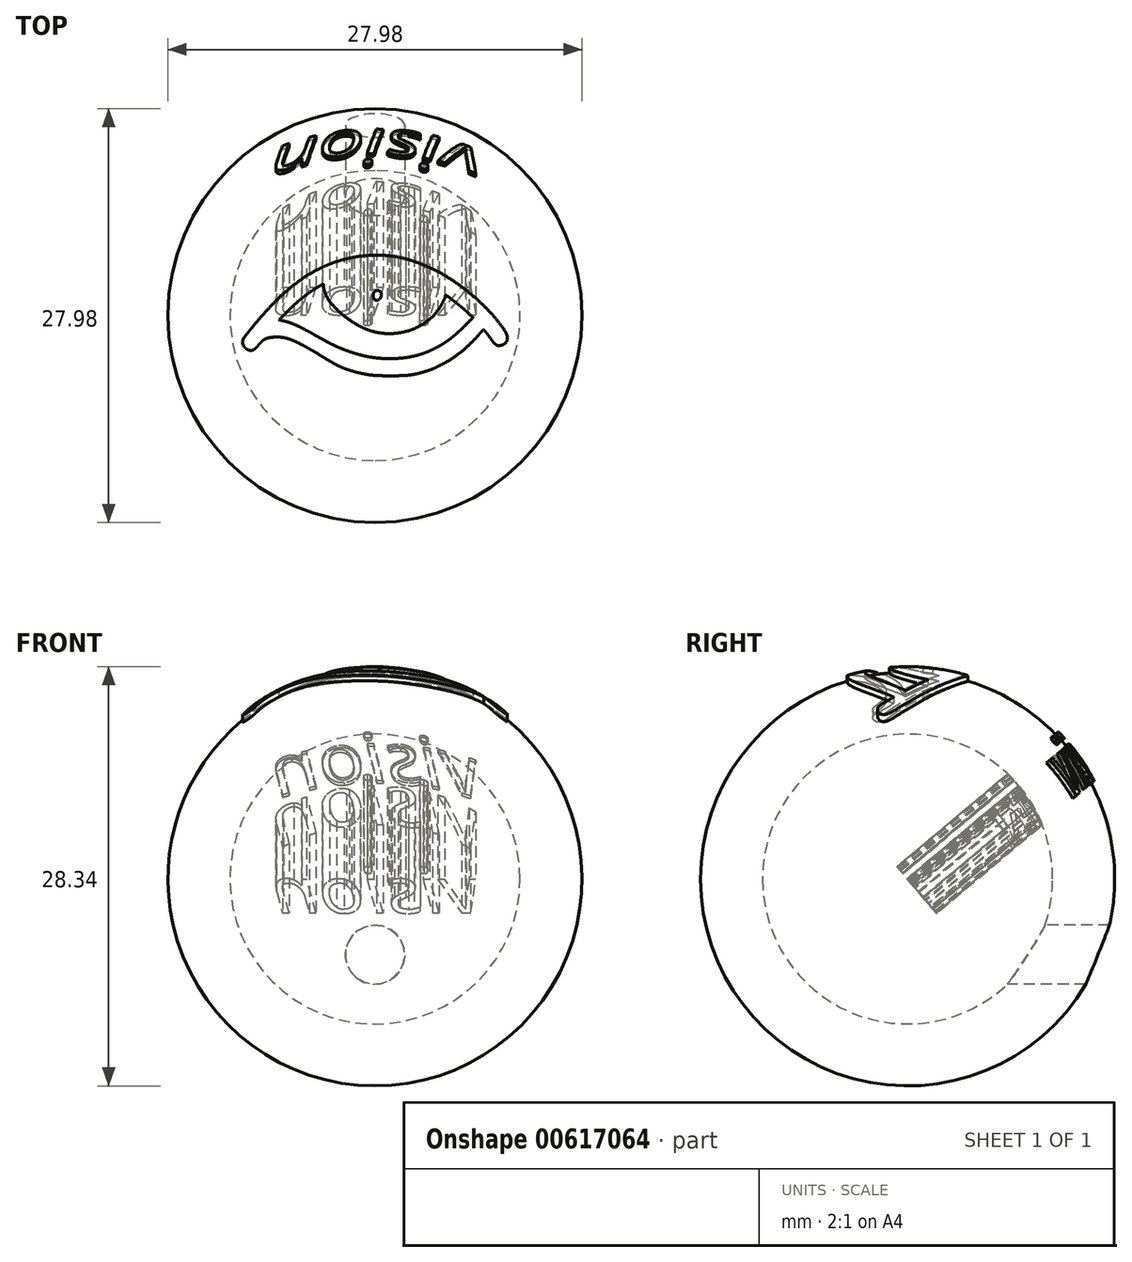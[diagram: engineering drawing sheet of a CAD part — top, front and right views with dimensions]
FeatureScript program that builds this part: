
annotation { "Feature Type Name" : "Feature", "Feature Type Description" : "" }
export const myFeature = defineFeature(function(context is Context, id is Id, definition is map)
    precondition{}
    {
        {
            var Q0;
            Q0=qCreatedBy(makeId("Top.planeOp"),FACE);
            var sketch = newSketch(context, id + "F0", { "sketchPlane" : qUnion([Q0])});
            skLineSegment(sketch, "E0", {"start": v(0, -10) * mm, "end": v(0, 10) * mm});
            skArc(sketch, "E1", {"start": v(0, 10) * mm, "mid": v(-10, 0) * mm, "end": v(0, -10) * mm});
            skSolve(sketch);
        }
        {
            var Q0;
            {var subQ0=sQuery(id+"F0.wireOp",EDGE,"E1");Q0=makeQuery(id+"F0.imprint","IMPRINT",FACE,{"disambiguationData":[TD([[makeQuery(id+"F0.imprint","IMPRINT",EDGE,{"derivedFrom":subQ0}),1.0]])]});}
            var Q1;
            Q1=sQuery(id+"F0.wireOp",EDGE,"E0");
            revolve(context, id + "F1", {"entities" : qUnion([Q0]), "axis" : qUnion([Q1]), "revolveType" : RevolveType.FULL});
        }
        {
            var Q0;
            Q0=makeQuery(id+"F1.opRevolve","SWEPT_BODY",BODY,{"disambiguationData":[OSD([sQuery(id+"F0.wireOp",EDGE,"E0"),sQuery(id+"F0.wireOp",EDGE,"E1")])]});
            var Q1;
            Q1=sQuery(id+"F0.wireOp",VERTEX,"NPe4G0ez-t7S9-9isL-QO5v-uuJu600mHcIT.center");
            var Q2;
            Q2=sQuery(id+"F0.wireOp",VERTEX,"E1.center");
            transform(context, id + "F2", {"entities" : qUnion([Q0]), "transformType" : TransformType.SCALE_UNIFORMLY, "scale" : 33.3, "scalePoint" : qUnion([Q2]), "makeCopy" : false});
        }
        {
            var Q0;
            Q0=qCreatedBy(makeId("Top.planeOp"),FACE);
            var sketch = newSketch(context, id + "F3", { "sketchPlane" : qUnion([Q0])});
            skArc(sketch, "E2", {"start": v(-15.7, 96.27) * mm, "mid": v(-24.88, 95.28) * mm, "end": v(-34, 93.81) * mm});
            skArc(sketch, "E3", {"start": v(-34, 93.81) * mm, "mid": v(-43.55, 91.8) * mm, "end": v(-53.01, 89.37) * mm});
            skArc(sketch, "E4", {"start": v(-53.01, 89.37) * mm, "mid": v(-62.4, 86.52) * mm, "end": v(-71.64, 83.27) * mm});
            skArc(sketch, "E5", {"start": v(-71.64, 83.27) * mm, "mid": v(-80.3, 79.75) * mm, "end": v(-88.77, 75.81) * mm});
            skArc(sketch, "E6", {"start": v(-88.77, 75.81) * mm, "mid": v(-102.81, 68.2) * mm, "end": v(-116.28, 59.63) * mm});
            skArc(sketch, "E7", {"start": v(-116.28, 59.63) * mm, "mid": v(-129.86, 49.68) * mm, "end": v(-142.83, 38.92) * mm});
            skArc(sketch, "E8", {"start": v(-142.83, 38.92) * mm, "mid": v(-156.87, 25.88) * mm, "end": v(-170.22, 12.13) * mm});
            skArc(sketch, "E9", {"start": v(-170.22, 12.13) * mm, "mid": v(-185.55, -5) * mm, "end": v(-200.36, -22.6) * mm});
            skArc(sketch, "E10", {"start": v(-200.36, -22.6) * mm, "mid": v(-204.26, -27.4) * mm, "end": v(-208.11, -32.22) * mm});
            skArc(sketch, "E11", {"start": v(-208.11, -32.22) * mm, "mid": v(-209.68, -34.33) * mm, "end": v(-211.1, -36.54) * mm});
            skArc(sketch, "E12", {"start": v(-211.1, -36.54) * mm, "mid": v(-211.9, -38.1) * mm, "end": v(-212.43, -39.77) * mm});
            skArc(sketch, "E13", {"start": v(-212.43, -39.77) * mm, "mid": v(-212.77, -41.62) * mm, "end": v(-212.89, -43.5) * mm});
            skArc(sketch, "E14", {"start": v(-212.89, -43.5) * mm, "mid": v(-212.7, -45.36) * mm, "end": v(-212.17, -47.16) * mm});
            skArc(sketch, "E15", {"start": v(-212.17, -47.16) * mm, "mid": v(-211.25, -49.03) * mm, "end": v(-210.08, -50.75) * mm});
            skArc(sketch, "E16", {"start": v(-210.08, -50.75) * mm, "mid": v(-208.63, -52.35) * mm, "end": v(-206.98, -53.74) * mm});
            skArc(sketch, "E17", {"start": v(-206.98, -53.74) * mm, "mid": v(-205.23, -54.82) * mm, "end": v(-203.34, -55.62) * mm});
            skArc(sketch, "E18", {"start": v(-203.34, -55.62) * mm, "mid": v(-201.34, -56.09) * mm, "end": v(-199.3, -56.2) * mm});
            skArc(sketch, "E19", {"start": v(-199.3, -56.2) * mm, "mid": v(-197.43, -55.94) * mm, "end": v(-195.66, -55.27) * mm});
            skArc(sketch, "E20", {"start": v(-195.66, -55.27) * mm, "mid": v(-193.67, -54.05) * mm, "end": v(-191.9, -52.53) * mm});
            skArc(sketch, "E21", {"start": v(-191.9, -52.53) * mm, "mid": v(-189.54, -50.04) * mm, "end": v(-187.31, -47.43) * mm});
            skArc(sketch, "E22", {"start": v(-187.31, -47.43) * mm, "mid": v(-184.58, -44.29) * mm, "end": v(-181.61, -41.36) * mm});
            skArc(sketch, "E23", {"start": v(-181.61, -41.36) * mm, "mid": v(-179.01, -39.32) * mm, "end": v(-176.14, -37.68) * mm});
            skArc(sketch, "E24", {"start": v(-176.14, -37.68) * mm, "mid": v(-172.97, -36.44) * mm, "end": v(-169.65, -35.65) * mm});
            skArc(sketch, "E25", {"start": v(-169.65, -35.65) * mm, "mid": v(-165.2, -35.07) * mm, "end": v(-160.72, -34.76) * mm});
            skArc(sketch, "E26", {"start": v(-160.72, -34.76) * mm, "mid": v(-158.15, -34.7) * mm, "end": v(-155.59, -34.7) * mm});
            skArc(sketch, "E27", {"start": v(-155.59, -34.7) * mm, "mid": v(-153.46, -34.78) * mm, "end": v(-151.33, -34.94) * mm});
            skArc(sketch, "E28", {"start": v(-151.33, -34.94) * mm, "mid": v(-149.29, -35.18) * mm, "end": v(-147.26, -35.51) * mm});
            skArc(sketch, "E29", {"start": v(-147.26, -35.51) * mm, "mid": v(-144.98, -35.98) * mm, "end": v(-142.72, -36.5) * mm});
            skArc(sketch, "E30", {"start": v(-142.72, -36.5) * mm, "mid": v(-137.7, -37.98) * mm, "end": v(-132.83, -39.85) * mm});
            skArc(sketch, "E31", {"start": v(-132.83, -39.85) * mm, "mid": v(-126.18, -42.83) * mm, "end": v(-119.62, -46) * mm});
            skArc(sketch, "E32", {"start": v(-119.62, -46) * mm, "mid": v(-111.94, -50) * mm, "end": v(-104.36, -54.22) * mm});
            skArc(sketch, "E33", {"start": v(-104.36, -54.22) * mm, "mid": v(-96.08, -59.09) * mm, "end": v(-87.89, -64.12) * mm});
            skArc(sketch, "E34", {"start": v(-87.89, -64.12) * mm, "mid": v(-78.64, -69.83) * mm, "end": v(-69.3, -75.4) * mm});
            skArc(sketch, "E35", {"start": v(-69.3, -75.4) * mm, "mid": v(-62.78, -79.02) * mm, "end": v(-56.09, -82.33) * mm});
            skArc(sketch, "E36", {"start": v(-56.09, -82.33) * mm, "mid": v(-50.08, -84.92) * mm, "end": v(-43.94, -87.15) * mm});
            skArc(sketch, "E37", {"start": v(-43.94, -87.15) * mm, "mid": v(-36.7, -89.4) * mm, "end": v(-29.39, -91.38) * mm});
            skArc(sketch, "E38", {"start": v(-29.39, -91.38) * mm, "mid": v(-22.75, -92.95) * mm, "end": v(-16.08, -94.33) * mm});
            skArc(sketch, "E39", {"start": v(-16.08, -94.33) * mm, "mid": v(-10.4, -95.3) * mm, "end": v(-4.68, -96.02) * mm});
            skArc(sketch, "E40", {"start": v(-4.68, -96.02) * mm, "mid": v(1.7, -96.55) * mm, "end": v(8.07, -96.83) * mm});
            skArc(sketch, "E41", {"start": v(8.07, -96.83) * mm, "mid": v(17.1, -97) * mm, "end": v(26.11, -97.06) * mm});
            skArc(sketch, "E42", {"start": v(26.11, -97.06) * mm, "mid": v(34.81, -96.98) * mm, "end": v(43.5, -96.78) * mm});
            skArc(sketch, "E43", {"start": v(43.5, -96.78) * mm, "mid": v(49.38, -96.48) * mm, "end": v(55.24, -95.93) * mm});
            skArc(sketch, "E44", {"start": v(55.24, -95.93) * mm, "mid": v(60.42, -95.18) * mm, "end": v(65.57, -94.17) * mm});
            skArc(sketch, "E45", {"start": v(65.57, -94.17) * mm, "mid": v(71.73, -92.68) * mm, "end": v(77.85, -91.01) * mm});
            skArc(sketch, "E46", {"start": v(77.85, -91.01) * mm, "mid": v(89.65, -87.08) * mm, "end": v(101.1, -82.22) * mm});
            skArc(sketch, "E47", {"start": v(101.1, -82.22) * mm, "mid": v(112.52, -76.3) * mm, "end": v(123.5, -69.56) * mm});
            skArc(sketch, "E48", {"start": v(123.5, -69.56) * mm, "mid": v(134.48, -61.7) * mm, "end": v(144.89, -53.1) * mm});
            skArc(sketch, "E49", {"start": v(144.89, -53.1) * mm, "mid": v(155.3, -43.34) * mm, "end": v(165.12, -32.98) * mm});
            skLineSegment(sketch, "E50", {"start": v(165.12, -32.98) * mm, "end": v(174.6, -22.4) * mm});
            skLineSegment(sketch, "E51", {"start": v(174.6, -22.4) * mm, "end": v(177.93, -26.25) * mm});
            skArc(sketch, "E52", {"start": v(177.93, -26.25) * mm, "mid": v(178.76, -27.23) * mm, "end": v(179.56, -28.24) * mm});
            skArc(sketch, "E53", {"start": v(179.56, -28.24) * mm, "mid": v(180.69, -29.73) * mm, "end": v(181.8, -31.22) * mm});
            skArc(sketch, "E54", {"start": v(181.8, -31.22) * mm, "mid": v(183.01, -32.88) * mm, "end": v(184.21, -34.54) * mm});
            skArc(sketch, "E55", {"start": v(184.21, -34.54) * mm, "mid": v(185.33, -36.15) * mm, "end": v(186.44, -37.76) * mm});
            skArc(sketch, "E56", {"start": v(186.44, -37.76) * mm, "mid": v(188.89, -41.17) * mm, "end": v(191.53, -44.43) * mm});
            skArc(sketch, "E57", {"start": v(191.53, -44.43) * mm, "mid": v(193.5, -46.3) * mm, "end": v(195.78, -47.72) * mm});
            skArc(sketch, "E58", {"start": v(195.78, -47.72) * mm, "mid": v(197.94, -48.43) * mm, "end": v(200.2, -48.52) * mm});
            skArc(sketch, "E59", {"start": v(200.2, -48.52) * mm, "mid": v(202.97, -48.04) * mm, "end": v(205.62, -47.16) * mm});
            skArc(sketch, "E60", {"start": v(205.62, -47.16) * mm, "mid": v(208.3, -45.62) * mm, "end": v(210.53, -43.46) * mm});
            skArc(sketch, "E61", {"start": v(210.53, -43.46) * mm, "mid": v(212.04, -40.9) * mm, "end": v(212.79, -38.01) * mm});
            skArc(sketch, "E62", {"start": v(212.79, -38.01) * mm, "mid": v(212.79, -34.58) * mm, "end": v(212.02, -31.24) * mm});
            skArc(sketch, "E63", {"start": v(212.02, -31.24) * mm, "mid": v(210.38, -27.4) * mm, "end": v(208.26, -23.82) * mm});
            skArc(sketch, "E64", {"start": v(208.26, -23.82) * mm, "mid": v(196.57, -8.01) * mm, "end": v(183.65, 6.8) * mm});
            skArc(sketch, "E65", {"start": v(183.65, 6.8) * mm, "mid": v(168.5, 21.85) * mm, "end": v(152.44, 35.92) * mm});
            skArc(sketch, "E66", {"start": v(152.44, 35.92) * mm, "mid": v(135.48, 49) * mm, "end": v(117.73, 60.98) * mm});
            skArc(sketch, "E67", {"start": v(117.73, 60.98) * mm, "mid": v(100.55, 70.9) * mm, "end": v(82.64, 79.43) * mm});
            skArc(sketch, "E68", {"start": v(82.64, 79.43) * mm, "mid": v(70.04, 84.47) * mm, "end": v(57.22, 88.9) * mm});
            skArc(sketch, "E69", {"start": v(57.22, 88.9) * mm, "mid": v(45.56, 92.16) * mm, "end": v(33.7, 94.6) * mm});
            skArc(sketch, "E70", {"start": v(33.7, 94.6) * mm, "mid": v(21.92, 96.2) * mm, "end": v(10.05, 96.96) * mm});
            skArc(sketch, "E71", {"start": v(10.05, 96.96) * mm, "mid": v(-2.83, 96.97) * mm, "end": v(-15.7, 96.27) * mm});
            skArc(sketch, "E72", {"start": v(-82.87, 47.15) * mm, "mid": v(-82.82, 46.3) * mm, "end": v(-82.7, 45.47) * mm});
            skArc(sketch, "E73", {"start": v(-82.7, 45.47) * mm, "mid": v(-82.45, 44.2) * mm, "end": v(-82.17, 42.93) * mm});
            skArc(sketch, "E74", {"start": v(-82.17, 42.93) * mm, "mid": v(-81.8, 41.5) * mm, "end": v(-81.41, 40.08) * mm});
            skArc(sketch, "E75", {"start": v(-81.41, 40.08) * mm, "mid": v(-80.99, 38.7) * mm, "end": v(-80.52, 37.33) * mm});
            skArc(sketch, "E76", {"start": v(-80.52, 37.33) * mm, "mid": v(-75.98, 27.48) * mm, "end": v(-69.69, 18.65) * mm});
            skArc(sketch, "E77", {"start": v(-69.69, 18.65) * mm, "mid": v(-60.18, 8.6) * mm, "end": v(-49.8, -0.55) * mm});
            skArc(sketch, "E78", {"start": v(-49.8, -0.55) * mm, "mid": v(-38.08, -9.14) * mm, "end": v(-25.64, -16.65) * mm});
            skArc(sketch, "E79", {"start": v(-25.64, -16.65) * mm, "mid": v(-13.91, -22.11) * mm, "end": v(-1.6, -26.06) * mm});
            skArc(sketch, "E80", {"start": v(-1.6, -26.06) * mm, "mid": v(12.82, -28.6) * mm, "end": v(27.45, -29.03) * mm});
            skArc(sketch, "E81", {"start": v(27.45, -29.03) * mm, "mid": v(42.14, -27.34) * mm, "end": v(56.45, -23.6) * mm});
            skArc(sketch, "E82", {"start": v(56.45, -23.6) * mm, "mid": v(69.79, -17.97) * mm, "end": v(82.17, -10.47) * mm});
            skArc(sketch, "E83", {"start": v(82.17, -10.47) * mm, "mid": v(92.73, -1.58) * mm, "end": v(101.67, 8.94) * mm});
            skArc(sketch, "E84", {"start": v(101.67, 8.94) * mm, "mid": v(103.47, 11.6) * mm, "end": v(105.14, 14.32) * mm});
            skArc(sketch, "E85", {"start": v(105.14, 14.32) * mm, "mid": v(107.13, 17.86) * mm, "end": v(109.03, 21.44) * mm});
            skArc(sketch, "E86", {"start": v(109.03, 21.44) * mm, "mid": v(110.8, 24.92) * mm, "end": v(112.5, 28.44) * mm});
            skArc(sketch, "E87", {"start": v(112.5, 28.44) * mm, "mid": v(112.96, 29.75) * mm, "end": v(113.11, 31.12) * mm});
            skArc(sketch, "E88", {"start": v(113.11, 31.12) * mm, "mid": v(113.13, 31.37) * mm, "end": v(113.17, 31.61) * mm});
            skArc(sketch, "E89", {"start": v(113.17, 31.61) * mm, "mid": v(113.24, 31.83) * mm, "end": v(113.34, 32.03) * mm});
            skArc(sketch, "E90", {"start": v(113.34, 32.03) * mm, "mid": v(113.46, 32.18) * mm, "end": v(113.6, 32.3) * mm});
            skArc(sketch, "E91", {"start": v(113.6, 32.3) * mm, "mid": v(113.74, 32.38) * mm, "end": v(113.9, 32.4) * mm});
            skArc(sketch, "E92", {"start": v(113.9, 32.4) * mm, "mid": v(115.02, 32.21) * mm, "end": v(116.02, 31.67) * mm});
            skArc(sketch, "E93", {"start": v(116.02, 31.67) * mm, "mid": v(122.38, 26.73) * mm, "end": v(128.73, 21.77) * mm});
            skArc(sketch, "E94", {"start": v(128.73, 21.77) * mm, "mid": v(134.7, 17.03) * mm, "end": v(140.62, 12.21) * mm});
            skArc(sketch, "E95", {"start": v(140.62, 12.21) * mm, "mid": v(144.67, 8.76) * mm, "end": v(148.6, 5.17) * mm});
            skLineSegment(sketch, "E96", {"start": v(148.6, 5.17) * mm, "end": v(157.59, -3.31) * mm});
            skLineSegment(sketch, "E97", {"start": v(157.59, -3.31) * mm, "end": v(142.6, -18.24) * mm});
            skArc(sketch, "E98", {"start": v(142.6, -18.24) * mm, "mid": v(136.78, -23.9) * mm, "end": v(130.82, -29.4) * mm});
            skArc(sketch, "E99", {"start": v(130.82, -29.4) * mm, "mid": v(125.67, -33.85) * mm, "end": v(120.33, -38.08) * mm});
            skArc(sketch, "E100", {"start": v(120.33, -38.08) * mm, "mid": v(115.17, -41.8) * mm, "end": v(109.84, -45.3) * mm});
            skArc(sketch, "E101", {"start": v(109.84, -45.3) * mm, "mid": v(104.04, -48.75) * mm, "end": v(98.11, -51.97) * mm});
            skArc(sketch, "E102", {"start": v(98.11, -51.97) * mm, "mid": v(90.09, -55.89) * mm, "end": v(81.87, -59.38) * mm});
            skArc(sketch, "E103", {"start": v(81.87, -59.38) * mm, "mid": v(73.97, -62.22) * mm, "end": v(65.92, -64.57) * mm});
            skArc(sketch, "E104", {"start": v(65.92, -64.57) * mm, "mid": v(57.65, -66.43) * mm, "end": v(49.28, -67.79) * mm});
            skArc(sketch, "E105", {"start": v(49.28, -67.79) * mm, "mid": v(40.14, -68.76) * mm, "end": v(30.96, -69.3) * mm});
            skArc(sketch, "E106", {"start": v(30.96, -69.3) * mm, "mid": v(21.95, -69.42) * mm, "end": v(12.94, -69.14) * mm});
            skArc(sketch, "E107", {"start": v(12.94, -69.14) * mm, "mid": v(4.36, -68.5) * mm, "end": v(-4.18, -67.41) * mm});
            skArc(sketch, "E108", {"start": v(-4.18, -67.41) * mm, "mid": v(-12.76, -65.9) * mm, "end": v(-21.27, -63.98) * mm});
            skArc(sketch, "E109", {"start": v(-21.27, -63.98) * mm, "mid": v(-30.29, -61.5) * mm, "end": v(-39.2, -58.7) * mm});
            skArc(sketch, "E110", {"start": v(-39.2, -58.7) * mm, "mid": v(-46.15, -56.25) * mm, "end": v(-53.02, -53.62) * mm});
            skArc(sketch, "E111", {"start": v(-53.02, -53.62) * mm, "mid": v(-59.24, -51.03) * mm, "end": v(-65.37, -48.24) * mm});
            skArc(sketch, "E112", {"start": v(-65.37, -48.24) * mm, "mid": v(-72.4, -44.77) * mm, "end": v(-79.33, -41.12) * mm});
            skArc(sketch, "E113", {"start": v(-79.33, -41.12) * mm, "mid": v(-89.08, -35.75) * mm, "end": v(-98.78, -30.3) * mm});
            skArc(sketch, "E114", {"start": v(-98.78, -30.3) * mm, "mid": v(-106.38, -26.03) * mm, "end": v(-114.04, -21.88) * mm});
            skArc(sketch, "E115", {"start": v(-114.04, -21.88) * mm, "mid": v(-119.86, -18.9) * mm, "end": v(-125.78, -16.1) * mm});
            skArc(sketch, "E116", {"start": v(-125.78, -16.1) * mm, "mid": v(-130.73, -13.97) * mm, "end": v(-135.75, -12.05) * mm});
            skArc(sketch, "E117", {"start": v(-135.75, -12.05) * mm, "mid": v(-140.5, -10.48) * mm, "end": v(-145.33, -9.16) * mm});
            skLineSegment(sketch, "E118", {"start": v(-145.33, -9.16) * mm, "end": v(-154.28, -6.95) * mm});
            skLineSegment(sketch, "E119", {"start": v(-154.28, -6.95) * mm, "end": v(-140.33, 7) * mm});
            skArc(sketch, "E120", {"start": v(-140.33, 7) * mm, "mid": v(-135.38, 11.87) * mm, "end": v(-130.35, 16.68) * mm});
            skArc(sketch, "E121", {"start": v(-130.35, 16.68) * mm, "mid": v(-125.96, 20.72) * mm, "end": v(-121.47, 24.66) * mm});
            skArc(sketch, "E122", {"start": v(-121.47, 24.66) * mm, "mid": v(-117.31, 28.12) * mm, "end": v(-113.07, 31.47) * mm});
            skArc(sketch, "E123", {"start": v(-113.07, 31.47) * mm, "mid": v(-108.85, 34.62) * mm, "end": v(-104.55, 37.63) * mm});
            skArc(sketch, "E124", {"start": v(-104.55, 37.63) * mm, "mid": v(-101.45, 39.71) * mm, "end": v(-98.31, 41.75) * mm});
            skArc(sketch, "E125", {"start": v(-98.31, 41.75) * mm, "mid": v(-94.91, 43.9) * mm, "end": v(-91.49, 46.02) * mm});
            skArc(sketch, "E126", {"start": v(-91.49, 46.02) * mm, "mid": v(-88.18, 48.02) * mm, "end": v(-84.86, 50.02) * mm});
            skArc(sketch, "E127", {"start": v(-84.86, 50.02) * mm, "mid": v(-84.27, 50.28) * mm, "end": v(-83.64, 50.38) * mm});
            skArc(sketch, "E128", {"start": v(-83.64, 50.38) * mm, "mid": v(-83.46, 50.33) * mm, "end": v(-83.34, 50.19) * mm});
            skArc(sketch, "E129", {"start": v(-83.34, 50.19) * mm, "mid": v(-83.2, 49.82) * mm, "end": v(-83.1, 49.44) * mm});
            skArc(sketch, "E130", {"start": v(-83.1, 49.44) * mm, "mid": v(-83, 48.92) * mm, "end": v(-82.93, 48.4) * mm});
            skArc(sketch, "E131", {"start": v(-82.93, 48.4) * mm, "mid": v(-82.88, 47.77) * mm, "end": v(-82.87, 47.15) * mm});
            skArc(sketch, "E132", {"start": v(7.9, 38.84) * mm, "mid": v(8.45, 38.4) * mm, "end": v(8.95, 37.88) * mm});
            skArc(sketch, "E133", {"start": v(8.95, 37.88) * mm, "mid": v(9.33, 37.35) * mm, "end": v(9.63, 36.75) * mm});
            skArc(sketch, "E134", {"start": v(9.63, 36.75) * mm, "mid": v(9.86, 36.04) * mm, "end": v(10, 35.3) * mm});
            skArc(sketch, "E135", {"start": v(10, 35.3) * mm, "mid": v(10.08, 34.3) * mm, "end": v(10.11, 33.3) * mm});
            skArc(sketch, "E136", {"start": v(10.11, 33.3) * mm, "mid": v(9.67, 30.37) * mm, "end": v(8.37, 27.7) * mm});
            skArc(sketch, "E137", {"start": v(8.37, 27.7) * mm, "mid": v(6.42, 25.77) * mm, "end": v(3.9, 24.69) * mm});
            skArc(sketch, "E138", {"start": v(3.9, 24.69) * mm, "mid": v(1.5, 24.73) * mm, "end": v(-0.63, 25.85) * mm});
            skArc(sketch, "E139", {"start": v(-0.63, 25.85) * mm, "mid": v(-2.2, 27.9) * mm, "end": v(-2.9, 30.4) * mm});
            skArc(sketch, "E140", {"start": v(-2.9, 30.4) * mm, "mid": v(-3, 31.9) * mm, "end": v(-3.03, 33.4) * mm});
            skArc(sketch, "E141", {"start": v(-3.03, 33.4) * mm, "mid": v(-2.96, 34.37) * mm, "end": v(-2.77, 35.32) * mm});
            skArc(sketch, "E142", {"start": v(-2.77, 35.32) * mm, "mid": v(-2.47, 36.1) * mm, "end": v(-2.05, 36.83) * mm});
            skArc(sketch, "E143", {"start": v(-2.05, 36.83) * mm, "mid": v(-1.4, 37.63) * mm, "end": v(-0.7, 38.36) * mm});
            skArc(sketch, "E144", {"start": v(-0.7, 38.36) * mm, "mid": v(0.26, 39.13) * mm, "end": v(1.32, 39.75) * mm});
            skArc(sketch, "E145", {"start": v(1.32, 39.75) * mm, "mid": v(2.35, 40.14) * mm, "end": v(3.44, 40.31) * mm});
            skArc(sketch, "E146", {"start": v(3.44, 40.31) * mm, "mid": v(4.56, 40.26) * mm, "end": v(5.64, 40) * mm});
            skArc(sketch, "E147", {"start": v(5.64, 40) * mm, "mid": v(6.8, 39.5) * mm, "end": v(7.9, 38.84) * mm});
            skSolve(sketch);
        }
        {
            var Q0;
            Q0=qSketchRegion(id+"F3",true);
            var Q1;
            Q1=sQuery(id+"F3.wireOp",EDGE,"c928f899-12af-4b01-b412-b3b7da3d830f");
            var Q2;
            Q2=sQuery(id+"F3.wireOp",EDGE,"b69f99c7-a6d0-4d1b-8752-9e82ab4c99ec");
            extrude(context, id + "F4", {"entities" : qUnion([Q0]), "operationType" : NewBodyOperationType.ADD, "surfaceEntities" : qUnion([Q1, Q2]), "depth" : 350 * mm});
        }
        {
            var Q0;
            Q0=makeQuery(id+"F4.opExtrude","SWEPT_BODY",BODY,{"disambiguationData":[OSD([sQuery(id+"F3.wireOp",EDGE,"15c6da4e-992d-4824-9d20-70d2d6be9970"),sQuery(id+"F3.wireOp",EDGE,"268c69ec-46be-456f-85eb-69decc32fe39"),sQuery(id+"F3.wireOp",EDGE,"1d386307-6059-4203-bca6-0c1cec3c82e1"),sQuery(id+"F3.wireOp",EDGE,"7d7c66d2-f869-427f-806b-ad436cacd60e"),sQuery(id+"F3.wireOp",EDGE,"1db91850-860e-493f-a3af-7a0f3f1512ae"),sQuery(id+"F3.wireOp",EDGE,"2c65f23b-9f03-4f6f-ab37-de452af29e3c"),sQuery(id+"F3.wireOp",EDGE,"ba006cbc-bbd7-44d9-84cc-9cde0967c280"),sQuery(id+"F3.wireOp",EDGE,"ae950208-c781-4a25-8fcf-ffe59b9085ff"),sQuery(id+"F3.wireOp",EDGE,"3cce0944-c62d-4831-9b9d-d1a418d328b4"),sQuery(id+"F3.wireOp",EDGE,"9edc5e7d-16c0-40c4-98ad-6b91d5df0e78"),sQuery(id+"F3.wireOp",EDGE,"aa452f44-44a2-4c64-bff5-a2a639df00db"),sQuery(id+"F3.wireOp",EDGE,"16259f99-ce20-4b7b-81e1-fa0909c03eb4"),sQuery(id+"F3.wireOp",EDGE,"79895566-a943-429d-b257-d76af3645bdf"),sQuery(id+"F3.wireOp",EDGE,"a85490ef-f17e-45c8-b92b-28215162778a"),sQuery(id+"F3.wireOp",EDGE,"322f1036-a6fd-4992-ab69-5919540af7a6"),sQuery(id+"F3.wireOp",EDGE,"0a87ff38-4ab4-4140-b3c3-2d7501d9f3b1"),sQuery(id+"F3.wireOp",EDGE,"a6e7bdf2-ef3e-49d4-9b3c-e34f5a41e0c4"),sQuery(id+"F3.wireOp",EDGE,"3e588790-576f-47c1-9730-f5e27fa1e8f9"),sQuery(id+"F3.wireOp",EDGE,"ce3739ef-15fd-4754-ad9c-ccf511a9a8fb"),sQuery(id+"F3.wireOp",EDGE,"201134a3-66f3-4a3f-aa9b-76948966efc0"),sQuery(id+"F3.wireOp",EDGE,"65b511ea-0759-428d-8070-88e1f521d8ea"),sQuery(id+"F3.wireOp",EDGE,"c37cddb6-5cf8-4891-aff4-7191a72080b9"),sQuery(id+"F3.wireOp",EDGE,"52a43dbd-e952-43e1-be3d-d70e107260e6"),sQuery(id+"F3.wireOp",EDGE,"08c1271f-f5c3-4f26-be27-7f5e21217dff"),sQuery(id+"F3.wireOp",EDGE,"59a09f58-0503-4180-962a-e04db21f0da8"),sQuery(id+"F3.wireOp",EDGE,"e56a4626-e956-42c3-bb5d-cd9dae1ca801"),sQuery(id+"F3.wireOp",EDGE,"5ff5d55f-af90-49eb-8040-353101557de8"),sQuery(id+"F3.wireOp",EDGE,"0ed7430b-e164-4f56-8af9-4534524aa7c0"),sQuery(id+"F3.wireOp",EDGE,"b5610a6e-b6bb-43e3-9a8d-d3d7c5f0098b"),sQuery(id+"F3.wireOp",EDGE,"1d417af8-88ad-47c2-a4e2-6fec82bd6695"),sQuery(id+"F3.wireOp",EDGE,"778ae99a-956a-4ddb-8078-d9bc57f9fc8e"),sQuery(id+"F3.wireOp",EDGE,"5b19af09-f144-446e-9dfa-8766819c9efd"),sQuery(id+"F3.wireOp",EDGE,"028339f6-0475-4a57-af8d-550e32ad7466"),sQuery(id+"F3.wireOp",EDGE,"d5ae35b6-d210-433a-92c8-e92622696872"),sQuery(id+"F3.wireOp",EDGE,"16a2e606-2caa-4876-9ffa-8f08c4ff3a37"),sQuery(id+"F3.wireOp",EDGE,"5b90b144-be56-4de7-a9dd-c1e0336acbe3"),sQuery(id+"F3.wireOp",EDGE,"5912d126-c5fc-41e4-bfb8-b4fefc52ca72"),sQuery(id+"F3.wireOp",EDGE,"2e96ce95-bd3e-4f27-a7f8-b62cf5efe954"),sQuery(id+"F3.wireOp",EDGE,"ecb4e259-1207-4dd0-bc3c-87c6506cc3a5"),sQuery(id+"F3.wireOp",EDGE,"105fb72e-4d79-4204-af2f-b3b26f5eb8d1"),sQuery(id+"F3.wireOp",EDGE,"fa59b598-df54-48c6-bb8f-c5f7618c69d0"),sQuery(id+"F3.wireOp",EDGE,"a6beef0d-f124-47ac-b957-e6cd3057a354"),sQuery(id+"F3.wireOp",EDGE,"7c3eaf53-dcb7-43b1-ad18-80ff953eb59e"),sQuery(id+"F3.wireOp",EDGE,"281fe206-104f-408f-94b6-be79f12604c9")])]});
            var Q1;
            Q1=makeQuery(id+"F4.opExtrude","SWEPT_BODY",BODY,{"disambiguationData":[OSD([sQuery(id+"F3.wireOp",EDGE,"58f6206a-5554-41d4-8cf7-6e0b4724a469"),sQuery(id+"F3.wireOp",EDGE,"85dabe77-b6aa-43d5-a519-64383616f71e"),sQuery(id+"F3.wireOp",EDGE,"4b679fe6-9e11-497d-b8fd-14ca14e49ddd"),sQuery(id+"F3.wireOp",EDGE,"51de25f6-d59e-4805-a327-1fd7e38869c8"),sQuery(id+"F3.wireOp",EDGE,"d47977fb-70d3-4df8-bc35-66fcc0e556e0"),sQuery(id+"F3.wireOp",EDGE,"235006b0-8f14-4ca2-82f0-f96b6b8c4766"),sQuery(id+"F3.wireOp",EDGE,"0fc7acd6-1c1d-47a8-ba12-62eb658d35ca"),sQuery(id+"F3.wireOp",EDGE,"883fa5e3-ca4c-4ce6-a249-4debf538fe24"),sQuery(id+"F3.wireOp",EDGE,"1da09ed1-22d9-43a1-a655-8acff5d61309"),sQuery(id+"F3.wireOp",EDGE,"32654a82-a09a-444f-bf73-45f818f0f235"),sQuery(id+"F3.wireOp",EDGE,"a398fd80-a0a9-4724-ba0e-1a7a000baa92"),sQuery(id+"F3.wireOp",EDGE,"f39f97c8-53f5-4046-9905-b28daecd4f10"),sQuery(id+"F3.wireOp",EDGE,"2484d883-0ec2-4c7d-9023-165ebbef226c"),sQuery(id+"F3.wireOp",EDGE,"f026d96f-3d32-4113-a1c9-3545f5cdbe4a"),sQuery(id+"F3.wireOp",EDGE,"974fee18-719e-4620-aace-d3676da2011b"),sQuery(id+"F3.wireOp",EDGE,"0c5766d2-a026-45af-bffd-0d1f783d5157"),sQuery(id+"F3.wireOp",EDGE,"5da13fee-9c04-45d8-805f-c7a03dde2383"),sQuery(id+"F3.wireOp",EDGE,"dbea32a3-85bd-4957-aef2-b6fe64a02f6b"),sQuery(id+"F3.wireOp",EDGE,"fba134ea-bf40-4191-ad8f-cc6b2b040a97"),sQuery(id+"F3.wireOp",EDGE,"0c19e200-7cd5-4fcb-83ed-261bd7936bc7"),sQuery(id+"F3.wireOp",EDGE,"246b843b-ea86-44e5-9cb9-335e6677b61d"),sQuery(id+"F3.wireOp",EDGE,"c1b3c9bc-1eb4-4c9b-99c8-0cebed89395a"),sQuery(id+"F3.wireOp",EDGE,"f93eebc3-1447-4029-8362-91325193ac2b"),sQuery(id+"F3.wireOp",EDGE,"bf86b12d-53a9-4c19-abaa-b1e658933ceb"),sQuery(id+"F3.wireOp",EDGE,"89646a71-1a60-4e14-b80a-74fb601d0855"),sQuery(id+"F3.wireOp",EDGE,"7b03dcde-0a52-4f3c-80e9-110d1d805e93"),sQuery(id+"F3.wireOp",EDGE,"83e8d1f3-8820-485b-8b6d-3ecd79124883"),sQuery(id+"F3.wireOp",EDGE,"ec7b56eb-ca95-44fd-a774-e9b7f9d3f50d"),sQuery(id+"F3.wireOp",EDGE,"31861aa6-cfd1-43ce-a7c5-bacfb7e2a30f"),sQuery(id+"F3.wireOp",EDGE,"fa3de647-1dd9-4141-982b-74ae8d07851d"),sQuery(id+"F3.wireOp",EDGE,"75d7c1c5-761c-4178-bfd4-4f469045899b"),sQuery(id+"F3.wireOp",EDGE,"4b3d7518-bd5d-4ecc-b2c5-d8dd665de4f4"),sQuery(id+"F3.wireOp",EDGE,"3be2682d-01bd-4f31-9cde-9df16a01e4a9"),sQuery(id+"F3.wireOp",EDGE,"72d3c7a9-2794-46eb-9b0d-6c526cc1b9a3"),sQuery(id+"F3.wireOp",EDGE,"0137e336-6b26-4f8d-b9ad-47ce1aa9eb31"),sQuery(id+"F3.wireOp",EDGE,"96000e4a-2d86-4b9f-af7d-a1c875cc048c"),sQuery(id+"F3.wireOp",EDGE,"139c5a79-9c0f-4e15-b57f-4c09662495a3"),sQuery(id+"F3.wireOp",EDGE,"8ea04d8b-b3da-46bb-9742-d8cba6b23bda"),sQuery(id+"F3.wireOp",EDGE,"b352b580-467e-481c-88ac-6217b8462947"),sQuery(id+"F3.wireOp",EDGE,"2503a493-1722-4539-8d54-7329fc0b116a"),sQuery(id+"F3.wireOp",EDGE,"a0615e06-0a48-4c65-8818-f0f693937022"),sQuery(id+"F3.wireOp",EDGE,"08389002-1ce8-438a-b5a4-698ca33590c2"),sQuery(id+"F3.wireOp",EDGE,"1756e4aa-c30a-461e-962c-81ee35d31e55"),sQuery(id+"F3.wireOp",EDGE,"5f84c249-07ea-4efb-9be3-ca494937f772"),sQuery(id+"F3.wireOp",EDGE,"cbefd041-b54f-4587-87b6-437b2290d1fc"),sQuery(id+"F3.wireOp",EDGE,"d44f58d4-f1a7-4aec-b016-8e7f1e498aeb"),sQuery(id+"F3.wireOp",EDGE,"0a5be90b-7545-44ea-9f2d-c726a5a2121c"),sQuery(id+"F3.wireOp",EDGE,"0cfaa442-d102-4580-8ef6-489f2aa1e6b3")])]});
            var Q2;
            Q2=makeQuery(id+"F4.opExtrude","SWEPT_BODY",BODY,{"disambiguationData":[OSD([sQuery(id+"F3.wireOp",EDGE,"9cc7aec6-4d94-4577-ab6c-32f5aa316238"),sQuery(id+"F3.wireOp",EDGE,"5ab2d840-4a32-405a-8c4b-a8126e3e1bc1"),sQuery(id+"F3.wireOp",EDGE,"56de48b4-9620-4637-8196-310e2641530f"),sQuery(id+"F3.wireOp",EDGE,"55327826-e64b-4830-85f2-3f22d36f43b5"),sQuery(id+"F3.wireOp",EDGE,"0245b46f-a639-4a95-8ca3-1568736ceed2"),sQuery(id+"F3.wireOp",EDGE,"9bd8a002-6ca7-4c84-8984-a620eefad103"),sQuery(id+"F3.wireOp",EDGE,"d4736c5e-da0b-46a0-ba9d-17ae07bb2b66"),sQuery(id+"F3.wireOp",EDGE,"125695b8-77e6-4e99-8f78-5f8fae1a0c71"),sQuery(id+"F3.wireOp",EDGE,"c9f25b10-a495-4684-8f25-8f255fabab6e"),sQuery(id+"F3.wireOp",EDGE,"0dbee67a-2ab6-4abb-ae16-0fe64d623848"),sQuery(id+"F3.wireOp",EDGE,"92c08d8e-ed2e-41a3-9c1a-b5ddaf8a0bf1"),sQuery(id+"F3.wireOp",EDGE,"00fabb15-0c1e-492e-85c1-17390e5b12bc"),sQuery(id+"F3.wireOp",EDGE,"065a9352-dddb-4e3f-b02a-444c867b75fe"),sQuery(id+"F3.wireOp",EDGE,"ef206bb6-e4f2-4189-9fc7-a7823c329ad6"),sQuery(id+"F3.wireOp",EDGE,"7199cbbe-c9bf-4cb9-b928-2ff8a84eb09e"),sQuery(id+"F3.wireOp",EDGE,"17bf9ed1-b881-4f74-816d-3511b6b328c7"),sQuery(id+"F3.wireOp",EDGE,"e5b615d0-4193-495d-b285-bd69ae30f000"),sQuery(id+"F3.wireOp",EDGE,"cfeaf62f-6be1-426b-9732-01e1a667be7e"),sQuery(id+"F3.wireOp",EDGE,"ac56344b-5ee6-4fa5-8e47-65b2a4ea3a01"),sQuery(id+"F3.wireOp",EDGE,"45b5fa53-15fd-43a0-91b0-943cc3286fc9")])]});
            var Q3;
            Q3=makeQuery(id+"F4.opExtrude","SWEPT_BODY",BODY,{"disambiguationData":[OSD([sQuery(id+"F3.wireOp",EDGE,"7bdfe37d-9957-4663-8239-5490fd3220d9"),sQuery(id+"F3.wireOp",EDGE,"6a91314f-c002-4565-bbf8-bb9f29165fb8"),sQuery(id+"F3.wireOp",EDGE,"b69f99c7-a6d0-4d1b-8752-9e82ab4c99ec"),sQuery(id+"F3.wireOp",EDGE,"c928f899-12af-4b01-b412-b3b7da3d830f"),sQuery(id+"F3.wireOp",EDGE,"ffa58721-cdd5-406d-be26-d96f7a050df4"),sQuery(id+"F3.wireOp",EDGE,"02fc7fb8-293b-44ff-ab78-63506d0aedb9"),sQuery(id+"F3.wireOp",EDGE,"147fb6cb-2565-4fb5-9280-6afbf9eef36b"),sQuery(id+"F3.wireOp",EDGE,"2cee3704-4124-415a-b391-31af1cf305d7"),sQuery(id+"F3.wireOp",EDGE,"32b2fb71-03c8-4978-9d95-2b5aaf044d0d"),sQuery(id+"F3.wireOp",EDGE,"e5d05796-7d6c-4350-8a4e-d55f5ade2f77"),sQuery(id+"F3.wireOp",EDGE,"77b1164c-8dd4-4680-b616-ac151a422eb2"),sQuery(id+"F3.wireOp",EDGE,"ec0798b8-0fbb-49ea-9766-39d2ee0936b0"),sQuery(id+"F3.wireOp",EDGE,"c4af6478-2a03-47a6-862f-c0c71886b8a3"),sQuery(id+"F3.wireOp",EDGE,"1912a38f-fa28-45c6-ab33-84cac2787056"),sQuery(id+"F3.wireOp",EDGE,"5d79fa95-f66d-4d2b-923b-4d54735f1fbd"),sQuery(id+"F3.wireOp",EDGE,"2db7aef4-a710-4bcf-9c1c-a8a87719953d"),sQuery(id+"F3.wireOp",EDGE,"183449de-345c-4115-9bca-43a403e62dbd"),sQuery(id+"F3.wireOp",EDGE,"e3ac8c9b-cab5-44b0-ad81-0e2b680c384a"),sQuery(id+"F3.wireOp",EDGE,"92e85db6-f458-41f6-a9a1-1e1a1a7e7809"),sQuery(id+"F3.wireOp",EDGE,"f0dbb46f-43a9-447b-9c75-8dfc9b95470d"),sQuery(id+"F3.wireOp",EDGE,"4b73f5f6-f769-4414-bdba-7d253e58fff4"),sQuery(id+"F3.wireOp",EDGE,"a88669dc-35b3-46bb-964f-c9bf6c4ab898"),sQuery(id+"F3.wireOp",EDGE,"2c559bae-f38f-4377-91e6-3c9de70acf11"),sQuery(id+"F3.wireOp",EDGE,"c1caf99b-adaa-42fe-a319-8cbcd819cf89"),sQuery(id+"F3.wireOp",EDGE,"54b04dd4-0ec4-4956-b19c-1141095738e3"),sQuery(id+"F3.wireOp",EDGE,"098f7a84-b7b8-4879-b21a-5c38879e4110"),sQuery(id+"F3.wireOp",EDGE,"b406a8e6-a226-4f3d-ac30-e4d06e4dac62"),sQuery(id+"F3.wireOp",EDGE,"36f95d1d-68ce-4231-ad71-3960c85e5915"),sQuery(id+"F3.wireOp",EDGE,"dc12cad8-2eed-454e-aa74-30099b1c9064"),sQuery(id+"F3.wireOp",EDGE,"4c78a4fd-cd81-43d6-85d6-6e4d3fbc1e98"),sQuery(id+"F3.wireOp",EDGE,"ee9e30de-787b-4e8f-b425-43a8e9289f81"),sQuery(id+"F3.wireOp",EDGE,"2518a3a4-c96b-4463-8704-0b71c65c60d2"),sQuery(id+"F3.wireOp",EDGE,"c9129a67-398c-4e37-92cb-2d54ff2e2e82"),sQuery(id+"F3.wireOp",EDGE,"d429d547-9f5b-42c6-bcca-effad2fa908f"),sQuery(id+"F3.wireOp",EDGE,"99d16e94-b2b3-43d5-9c7b-7bd463994dcb"),sQuery(id+"F3.wireOp",EDGE,"32993909-9a70-47ee-9097-89fff220f839"),sQuery(id+"F3.wireOp",EDGE,"6eabbeed-9496-4825-b168-63782a34f495"),sQuery(id+"F3.wireOp",EDGE,"f74987e3-8e60-4a5b-857f-839ae8aaf0cf"),sQuery(id+"F3.wireOp",EDGE,"1c218c86-035d-4441-93c0-9621d3297c3a"),sQuery(id+"F3.wireOp",EDGE,"0133f513-4b11-4cc4-b075-4625e9591e41"),sQuery(id+"F3.wireOp",EDGE,"fe921ad4-a8f5-4772-9aeb-350aca2e8948"),sQuery(id+"F3.wireOp",EDGE,"bfde0a4f-3cec-4f8e-8a23-dd1441b34c2b"),sQuery(id+"F3.wireOp",EDGE,"b41521ff-c5df-4b64-83ed-5e7635cf4438"),sQuery(id+"F3.wireOp",EDGE,"ed692599-6bbb-4379-8e89-ea326a0a0f87"),sQuery(id+"F3.wireOp",EDGE,"a98451c0-d76c-436e-99f9-a3fe9c8430a4"),sQuery(id+"F3.wireOp",EDGE,"561965b2-3050-4f49-9305-d98a2b852bbe"),sQuery(id+"F3.wireOp",EDGE,"e13dfa59-48e6-4b4e-94b9-1fc5254b0f2e"),sQuery(id+"F3.wireOp",EDGE,"0354e106-253a-4bfa-b5b7-b09cd0f2f6c0"),sQuery(id+"F3.wireOp",EDGE,"8df1dcc8-d00a-4777-85fd-8af8e9830bd1"),sQuery(id+"F3.wireOp",EDGE,"26ce3762-0d1a-4b81-9a23-debcfc24da1c"),sQuery(id+"F3.wireOp",EDGE,"3e900f8f-3ffb-4e32-b536-61fea2f3e30a"),sQuery(id+"F3.wireOp",EDGE,"4a1b5445-5559-461f-b6f1-b4cd9b95ea10")])]});
            var Q4;
            Q4=makeQuery(id+"F1.opRevolve","SWEPT_BODY",BODY,{"disambiguationData":[OSD([sQuery(id+"F0.wireOp",EDGE,"E0"),sQuery(id+"F0.wireOp",EDGE,"E1")])]});
            var Q5;
            Q5=qCreatedBy(makeId("Origin.pointOp"),VERTEX);
            transform(context, id + "F5", {"entities" : qUnion([Q0, Q1, Q2, Q3, Q4]), "transformType" : TransformType.SCALE_UNIFORMLY, "scale" : 0.03, "scalePoint" : qUnion([Q5]), "makeCopy" : false});
        }
        {
            var Q0;
            Q0=qCreatedBy(makeId("Top.planeOp"),FACE);
            var sketch = newSketch(context, id + "F6", { "sketchPlane" : qUnion([Q0])});
            skLineSegment(sketch, "E148", {"start": v(0, 15) * mm, "end": v(0, -15) * mm});
            skArc(sketch, "E149", {"start": v(0, 15) * mm, "mid": v(-15, 0) * mm, "end": v(0, -15) * mm});
            skArc(sketch, "E150", {"start": v(0, 10.25) * mm, "mid": v(-10.25, 0) * mm, "end": v(0, -10.25) * mm});
            skArc(sketch, "E151", {"start": v(0, 7) * mm, "mid": v(-7, 0) * mm, "end": v(0, -7) * mm});
            skSolve(sketch);
        }
        {
            var Q0;
            {var subQ0=sQuery(id+"F6.wireOp",EDGE,"E149");Q0=makeQuery(id+"F6.imprint","IMPRINT",FACE,{"disambiguationData":[TD([[makeQuery(id+"F6.imprint","IMPRINT",EDGE,{"derivedFrom":subQ0}),1.0]])]});}
            var Q1;
            {var subQ0=sQuery(id+"F6.wireOp",EDGE,"E151");Q1=makeQuery(id+"F6.imprint","IMPRINT",FACE,{"disambiguationData":[TD([[makeQuery(id+"F6.imprint","IMPRINT",EDGE,{"derivedFrom":subQ0}),1.0]])]});}
            var Q2;
            Q2=sQuery(id+"F6.wireOp",EDGE,"E148");
            revolve(context, id + "F7", {"operationType" : NewBodyOperationType.REMOVE, "entities" : qUnion([Q0, Q1]), "axis" : qUnion([Q2]), "revolveType" : RevolveType.FULL});
        }
        {
            var Q0;
            Q0=makeQuery(id+"F1.opRevolve","SWEPT_BODY",BODY,{"disambiguationData":[OSD([sQuery(id+"F0.wireOp",EDGE,"E0"),sQuery(id+"F0.wireOp",EDGE,"E1")])]});
            var Q1;
            Q1=sQuery(id+"F0.wireOp",VERTEX,"E1.center");
            transform(context, id + "F8", {"entities" : qUnion([Q0]), "transformType" : TransformType.SCALE_UNIFORMLY, "scale" : 1.4, "scalePoint" : qUnion([Q1]), "makeCopy" : false});
        }
        {
            var Q0;
            Q0=qCreatedBy(makeId("Front.planeOp"),FACE);
            var sketch = newSketch(context, id + "F9", { "sketchPlane" : qUnion([Q0])});
            skCircle(sketch, "E152", {"center": v(0, -5.12) * mm, "radius": 2 * mm});
            skSolve(sketch);
        }
        {
            var Q0;
            Q0=qSketchRegion(id+"F9",true);
            extrude(context, id + "F10", {"entities" : qUnion([Q0]), "operationType" : NewBodyOperationType.REMOVE, "oppositeDirection" : true, "depth" : 25 * mm});
        }
        {
            var Q0;
            Q0=qCreatedBy(makeId("Top.planeOp"),FACE);
            var sketch = newSketch(context, id + "F11", { "sketchPlane" : qUnion([Q0])});
            skLineSegment(sketch, "E153", {"start": v(-51.76, 0) * mm, "end": v(46.62, 0) * mm});
            skSolve(sketch);
        }
        {
            var Q0;
            Q0=sQuery(id+"F11.wireOp",EDGE,"E153");
            cPlane(context, id + "F12", {"entities" : qUnion([Q0]), "cplaneType" : CPlaneType.LINE_ANGLE, "offset" : 25 * mm, "angle" : 40 * degree, "width" : 150 * mm, "height" : 150 * mm});
        }
        {
            var Q0;
            Q0=qCreatedBy(id+"F12.planeOp",FACE);
            var sketch = newSketch(context, id + "F13", { "sketchPlane" : qUnion([Q0])});
            skText(sketch, "E154", { "text": "vision", "fontName": "OpenSans-Italic.ttf"});
            const initialGuessF13  = {"E154": [-0.00707, -0.003, 1, 0, 0.004]};
            skSetInitialGuess(sketch, initialGuessF13);
            skSolve(sketch);
        }
        {
            var Q0;
            Q0=qCreatedBy(makeId("Right.planeOp"),FACE);
            var sketch = newSketch(context, id + "F14", { "sketchPlane" : qUnion([Q0])});
            skArc(sketch, "E155", {"start": v(0, -14.25) * mm, "mid": v(-14.25, 0) * mm, "end": v(0, 14.25) * mm});
            skLineSegment(sketch, "E156", {"start": v(0, 14.25) * mm, "end": v(0, -14.25) * mm});
            skSolve(sketch);
        }
        {
            var Q0;
            Q0 = qSketchRegion(id + "F14", true);
            var Q1;
            Q1=sQuery(id+"F14.wireOp",EDGE,"E155");
            var Q2;
            Q2=sQuery(id+"F14.wireOp",EDGE,"E156");
            revolve(context, id + "F15", {"bodyType" : ToolBodyType.SURFACE, "entities" : qUnion([Q0]), "surfaceEntities" : qUnion([Q1]), "axis" : qUnion([Q2]), "revolveType" : RevolveType.FULL});
        }
        {
            var Q0;
            Q0 = qSketchRegion(id + "F13", true);
            var Q1;
            Q1=makeQuery(id+"F15.opRevolve","SWEPT_FACE",FACE,{"disambiguationData":[OSD([sQuery(id+"F14.wireOp",EDGE,"E155")])]});
            extrude(context, id + "F16", {"entities" : qUnion([Q0]), "operationType" : NewBodyOperationType.ADD, "endBound" : BoundingType.UP_TO_SURFACE, "depth" : 25 * mm, "endBoundEntityFace" : qUnion([Q1]), "offsetDistance" : 25 * mm});
        }
    });
